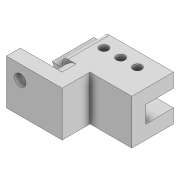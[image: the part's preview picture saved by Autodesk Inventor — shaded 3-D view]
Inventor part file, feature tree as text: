
AUTODESK INVENTOR PART (.ipt)
format: ipt  version: 2022 (Build 260153000, 153)  size: 214,528 bytes
history: native  units: mm
features: extrude x8, sketch x5, projected_geometry x5, pattern_linear x2, fillet x2, plane x1, mirror x1
ambient origin geometry x8: Origin, YZ Plane, XZ Plane, XY Plane, X Axis, Y Axis, Z Axis, Center Point
bodies: Solid1 (feature_tree)
feature tree (24):
  sketch  "Sketch2"  dims[d0=3.1mm d1=10.0mm]
  extrude  "Extrusion1"  Depth=10.0mm
  extrude  "Extrusion2"  Depth=30.0mm
  pattern_linear  "Rectangular Pattern1"  Count1=3 Spacing1=6.0mm
  pattern_linear  "Rectangular Pattern2"  Count1=2 Spacing1=11.1mm
  sketch  "Sketch3"  dims[d2=5.0mm d3=30.0mm]
  extrude  "Extrusion3"  Depth=5.0mm TaperAngle=0.0deg
  extrude  "Extrusion4"  Depth=2.0mm TaperAngle=0.0deg
  extrude  "Extrusion5"  Depth=10.0mm TaperAngle=0.0deg
  extrude  "Extrusion8"  Depth=2.0mm
  plane  "Work Plane2"
  mirror  "Mirror2"
  extrude  "Extrusion9"  Depth=5.0mm
  extrude  "Extrusion10"  Depth=5.0mm
  fillet  "Fillet1"  Radius=5.0mm
  fillet  "Fillet2"  Radius=5.0mm
  sketch  "Sketch5"  dims[d4=10.0mm]
  projected_geometry  "Projected Loop1"
  sketch  "Sketch6"  dims[d5=5.0mm d6=0.0mm]
  projected_geometry  "Projected Loop2"
  sketch  "Sketch7"  dims[d7=10.0mm d8=0.0mm d9=30.0mm d11=6.0mm d12=20.0mm d14=11.1mm d18=5.0mm d19=0.0mm d20=100.0mm d21=0.0mm d22=10.0mm d23=0.0mm d36=4.1mm d37=5.0mm d38=5.0mm d39=5.0mm d40=5.0mm d41=5.0mm d42=5.0mm d43=0.0mm d44=20.0mm d45=100.0mm d46=0.0mm d47=3.5mm d48=1.0mm d49=0.0mm d50=4.0mm d51=2.0mm]
  projected_geometry  "Projected Loop3"
  projected_geometry  "Project Cut Edges1"
  projected_geometry  "Project Cut Edges3"
